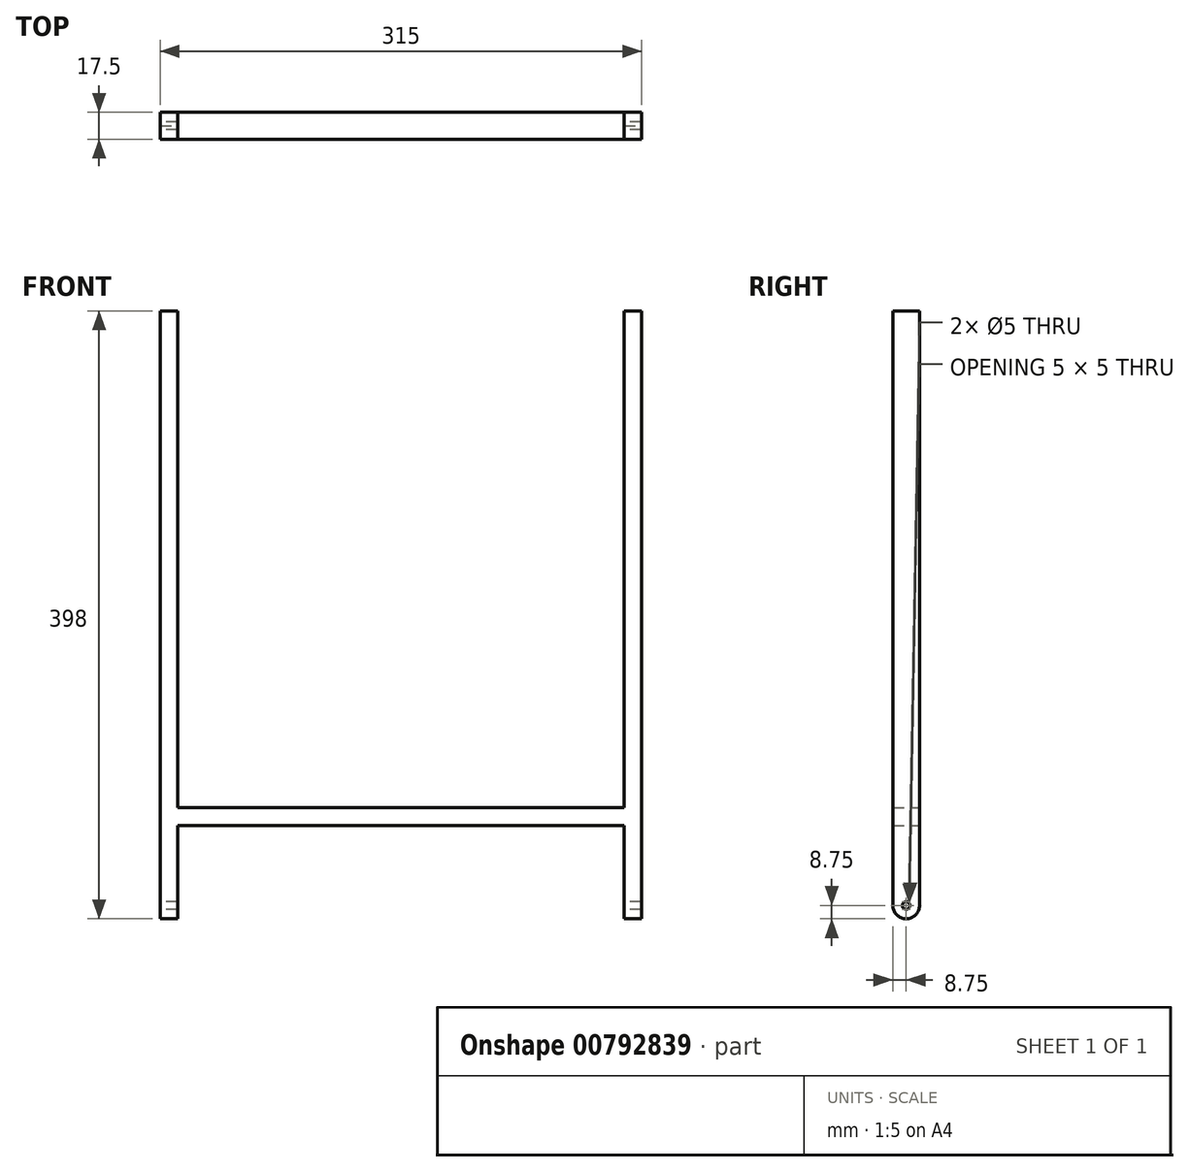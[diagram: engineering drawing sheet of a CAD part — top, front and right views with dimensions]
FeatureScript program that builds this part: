
annotation { "Feature Type Name" : "Feature", "Feature Type Description" : "" }
export const myFeature = defineFeature(function(context is Context, id is Id, definition is map)
    precondition{}
    {
        {
            var Q0;
            Q0=qCreatedBy(makeId("Front.planeOp"),FACE);
            var sketch = newSketch(context, id + "F0", { "sketchPlane" : qUnion([Q0])});
            skLineSegment(sketch, "E0", {"start": v(0, 214.27) * mm, "end": v(0, -242.24) * mm, "construction": true});
            skLineSegment(sketch, "E1", {"start": v(265.27, 0) * mm, "end": v(-309.68, 0) * mm, "construction": true});
            skLineSegment(sketch, "E2", {"start": v(0, -137.77) * mm, "end": v(146, -137.77) * mm});
            skLineSegment(sketch, "E3", {"start": v(146, -126.27) * mm, "end": v(0, -126.27) * mm});
            skLineSegment(sketch, "E4", {"start": v(146, -137.77) * mm, "end": v(146, -199) * mm});
            skLineSegment(sketch, "E5", {"start": v(146, -199) * mm, "end": v(157.5, -199) * mm});
            skLineSegment(sketch, "E6", {"start": v(157.5, -199) * mm, "end": v(157.5, 0) * mm});
            skLineSegment(sketch, "E7", {"start": v(146, -126.27) * mm, "end": v(146, 0) * mm});
            skLineSegment(sketch, "E8.MirrorCS", {"start": v(157.5, 199) * mm, "end": v(157.5, 0) * mm});
            skLineSegment(sketch, "E9.MirrorCS", {"start": v(146, 199) * mm, "end": v(157.5, 199) * mm});
            skLineSegment(sketch, "E10.MirrorCS", {"start": v(-146, -126.27) * mm, "end": v(0, -126.27) * mm});
            skLineSegment(sketch, "E11.MirrorCS", {"start": v(0, -137.77) * mm, "end": v(-146, -137.77) * mm});
            skLineSegment(sketch, "E12.MirrorCS", {"start": v(-146, -137.77) * mm, "end": v(-146, -199) * mm});
            skLineSegment(sketch, "E13.MirrorCS", {"start": v(-146, -199) * mm, "end": v(-157.5, -199) * mm});
            skLineSegment(sketch, "E14.MirrorCS", {"start": v(-157.5, -199) * mm, "end": v(-157.5, 0) * mm});
            skLineSegment(sketch, "E15.MirrorCS", {"start": v(-146, -126.27) * mm, "end": v(-146, 0) * mm});
            skLineSegment(sketch, "E16.MirrorCS", {"start": v(-157.5, 199) * mm, "end": v(-157.5, 0) * mm});
            skLineSegment(sketch, "E17.MirrorCS", {"start": v(-146, 199) * mm, "end": v(-157.5, 199) * mm});
            skLineSegment(sketch, "E18", {"start": v(146, 199) * mm, "end": v(146, 0) * mm});
            skLineSegment(sketch, "E19.MirrorCS", {"start": v(-146, 199) * mm, "end": v(-146, 0) * mm});
            skLineSegment(sketch, "E20", {"start": v(-6.46, -126.27) * mm, "end": v(8.7, -126.27) * mm});
            skSolve(sketch);
        }
        {
            var Q0;
            Q0 = qSketchRegion(id + "F0", true);
            extrude(context, id + "F1", {"entities" : qUnion([Q0]), "depth" : 17.5 * mm, "offsetDistance" : 25 * mm});
        }
        {
            var Q0;
            Q0=makeQuery(id+"F1.opExtrude","SWEPT_FACE",FACE,{"disambiguationData":[OSD([sQuery(id+"F0.wireOp",EDGE,"E14.MirrorCS"),sQuery(id+"F0.wireOp",EDGE,"E16.MirrorCS")])]});
            var sketch = newSketch(context, id + "F2", { "sketchPlane" : qUnion([Q0])});
            skLineSegment(sketch, "E21", {"start": v(8.75, -210.34) * mm, "end": v(8.75, -156.48) * mm, "construction": true});
            skPoint(sketch, "E21.startSnap0", {"position": v(8.75, -199) * mm});
            skLineSegment(sketch, "E22", {"start": v(-10.89, -190.25) * mm, "end": v(30.05, -190.25) * mm, "construction": true});
            skCircle(sketch, "E23", {"center": v(8.75, -190.25) * mm, "radius": 2.5 * mm});
            skSolve(sketch);
        }
        {
            var Q0;
            Q0 = qSketchRegion(id + "F2", true);
            extrude(context, id + "F3", {"entities" : qUnion([Q0]), "operationType" : NewBodyOperationType.REMOVE, "oppositeDirection" : true, "depth" : 335 * mm, "offsetDistance" : 25 * mm});
        }
        {
            var Q0;
            Q0=makeQuery(id+"F1.opExtrude","CAP_EDGE",EDGE,{"disambiguationData":[OSD([sQuery(id+"F0.wireOp",EDGE,"E13.MirrorCS")])],"isStart":true});
            var Q1;
            Q1=makeQuery(id+"F1.opExtrude","CAP_EDGE",EDGE,{"disambiguationData":[OSD([sQuery(id+"F0.wireOp",EDGE,"E5")])],"isStart":true});
            var Q2;
            Q2=makeQuery(id+"F1.opExtrude","CAP_EDGE",EDGE,{"disambiguationData":[OSD([sQuery(id+"F0.wireOp",EDGE,"E13.MirrorCS")])],"isStart":false});
            var Q3;
            Q3=makeQuery(id+"F1.opExtrude","CAP_EDGE",EDGE,{"disambiguationData":[OSD([sQuery(id+"F0.wireOp",EDGE,"E5")])],"isStart":false});
            fillet(context, id + "F4", {"entities" : qUnion([Q0, Q1, Q2, Q3]), "radius" : 9 * mm, "tangentPropagation" : true, "allowEdgeOverflow" : false});
        }
    });
